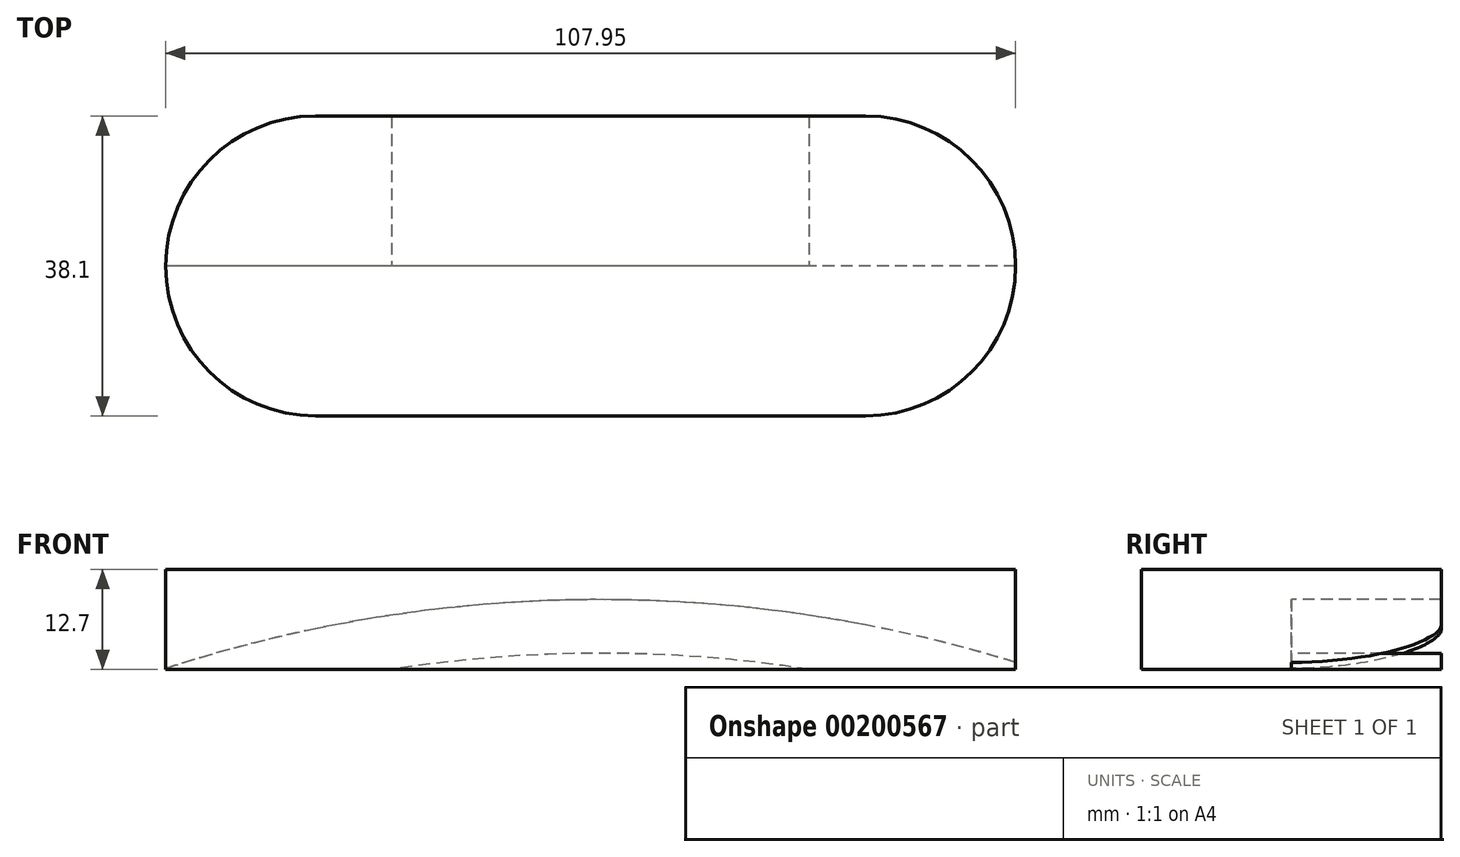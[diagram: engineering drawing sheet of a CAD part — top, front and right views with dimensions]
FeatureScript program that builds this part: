
annotation { "Feature Type Name" : "Feature", "Feature Type Description" : "" }
export const myFeature = defineFeature(function(context is Context, id is Id, definition is map)
    precondition{}
    {
        {
            var Q0;
            Q0=qCreatedBy(makeId("Top.planeOp"),FACE);
            var sketch = newSketch(context, id + "F0", { "sketchPlane" : qUnion([Q0])});
            skLineSegment(sketch, "E0.bottom", {"start": v(34.93, 19.05) * mm, "end": v(-34.92, 19.05) * mm});
            skLineSegment(sketch, "E0.top", {"start": v(34.92, -19.05) * mm, "end": v(-34.93, -19.05) * mm});
            skPoint(sketch, "E0.middle", {"position": v(0, 0) * mm});
            skArc(sketch, "E1", {"start": v(-34.92, 19.05) * mm, "mid": v(-53.98, 0) * mm, "end": v(-34.93, -19.05) * mm});
            skArc(sketch, "E2", {"start": v(34.92, -19.05) * mm, "mid": v(53.97, 0) * mm, "end": v(34.93, 19.05) * mm});
            skLineSegment(sketch, "E3", {"start": v(-34.93, 0) * mm, "end": v(34.92, 0) * mm, "construction": true});
            skSolve(sketch);
        }
        {
            var Q0;
            Q0=makeQuery(id+"F0.imprint","IMPRINT",FACE,{"disambiguationData":[TD([[makeQuery(id+"F0.imprint","IMPRINT",EDGE,{"derivedFrom":sQuery(id+"F0.wireOp",EDGE,"E0.bottom")}),1.0]])]});
            extrude(context, id + "F1", {"entities" : qUnion([Q0]), "depth" : 12.7 * mm});
        }
        {
            var Q0;
            Q0=qCreatedBy(makeId("Front.planeOp"),FACE);
            var sketch = newSketch(context, id + "F2", { "sketchPlane" : qUnion([Q0])});
            skArc(sketch, "E4", {"start": v(27.75, 0) * mm, "mid": v(1.23, 2.06) * mm, "end": v(-25.3, 0) * mm});
            skArc(sketch, "E5", {"start": v(56.8, 0) * mm, "mid": v(1.23, 8.87) * mm, "end": v(-54.35, 0) * mm});
            skLineSegment(sketch, "E6", {"start": v(56.8, 0) * mm, "end": v(27.75, 0) * mm});
            skLineSegment(sketch, "E7", {"start": v(-25.3, 0) * mm, "end": v(-54.35, 0) * mm});
            skSolve(sketch);
        }
        {
            var Q0;
            Q0 = qSketchRegion(id + "F2", true);
            extrude(context, id + "F3", {"entities" : qUnion([Q0]), "operationType" : NewBodyOperationType.REMOVE, "oppositeDirection" : true, "depth" : 50.8 * mm});
        }
    });
